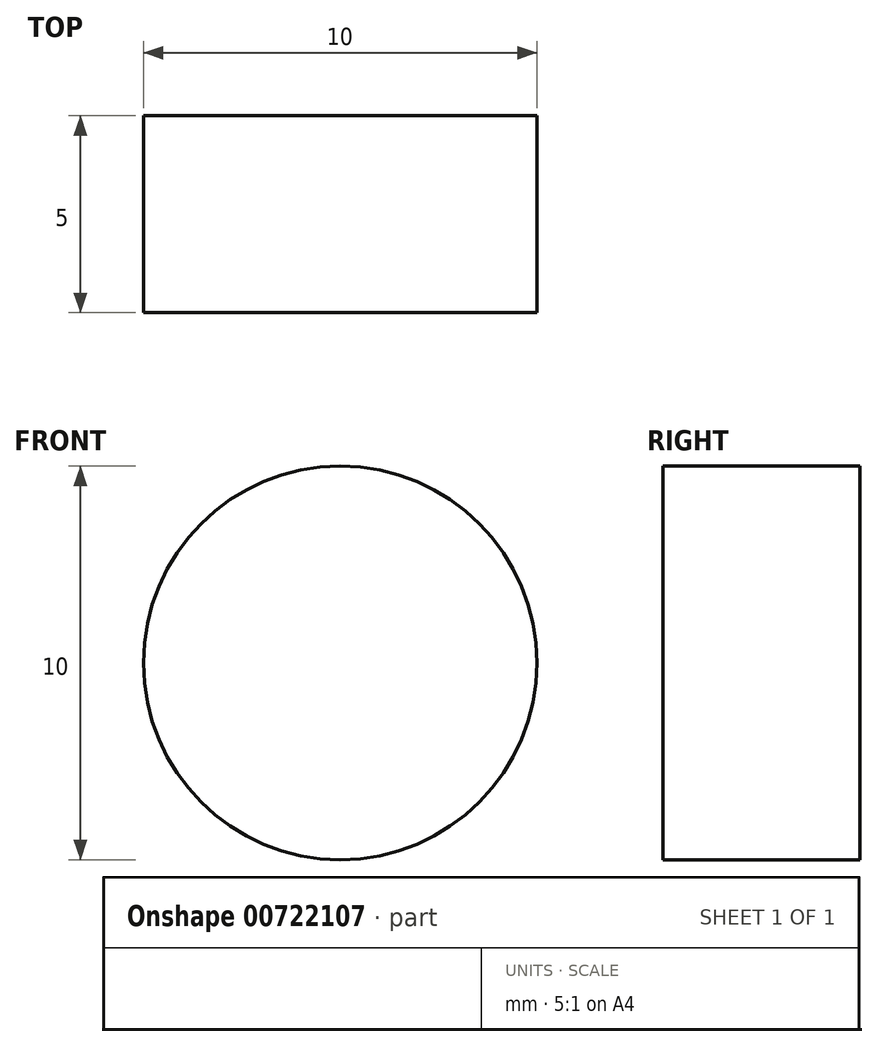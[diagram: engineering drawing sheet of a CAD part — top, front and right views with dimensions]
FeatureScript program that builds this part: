
annotation { "Feature Type Name" : "Feature", "Feature Type Description" : "" }
export const myFeature = defineFeature(function(context is Context, id is Id, definition is map)
    precondition{}
    {
        {
            var Q0;
            Q0=qCreatedBy(makeId("Front.planeOp"),FACE);
            var sketch = newSketch(context, id + "F0", { "sketchPlane" : qUnion([Q0])});
            skCircle(sketch, "E0", {"center": v(0, 0) * mm, "radius": 5 * mm});
            skSolve(sketch);
        }
        {
            var Q0;
            Q0 = qSketchRegion(id + "F0", true);
            extrude(context, id + "F1", {"entities" : qUnion([Q0]), "oppositeDirection" : true, "depth" : 5 * mm, "offsetDistance" : 25 * mm});
        }
    });
